# Revit family: Hager-VECTOR-Surface_mounted-IP65-With_Cover-With_DIN-NoHosted-PT-pt
name_source: partatom
category: Electrical Equipment
units: mm (PartAtom-declared; Revit-internal decimal feet)

## family parameters
Always vertical = Yes
Cut with Voids When Loaded = No
Maintain Annotation Orientation = No
Panel Configuration = Two Columns, Circuits Across
Part Type = Panelboard
Room Calculation Point = No
Round Connector Dimension = Use Diameter
Shared = No
Work Plane-Based = Yes

## types (22) — shared parameters
Code hager = ADD-EC000214_EU
Default Elevation = 1200 mm
EF000003 - Mounting method = Surface mounted
EF000024 - UV resistant = No
EF000116 - RAL-number = 7035
EF000118 - With mounting plate = No
EF001062 - EMC-version = No
EF001134 - DIN-rail = Yes
EF005474 - Degree of protection (IP) = IP65
EF006306 - With lock = No
EF015777 - Neutral terminal block = No
ETIM class code = EC000214
ETIM class name = Small distribution board
HG000001-Number of columns = 1
HG000002-With door or cover = Yes
HG000003-Range = VECTOR
HG000005-Thickness = 2 mm  [stored 0.00656168 ft]
HG000006-Flush mounted = No
HG000009-Double swing door = No
HG000010-Asymmetric doors = No
HG000011-Empty rows from bottom = No
HG000012-Door swing angle = 90.00°
HG000013-Door on the left = No
HG000014-Door on the right = Yes
HG000015-Clearance visibility = Yes
HG000016-Door 3D visibility = Yes
HG000017-Distance between poles = 18 mm  [stored 0.0590551 ft]
HG000060-RAL-number = 7035
HG000099-Onfly Template ID = 507532
Manufacturer = Hager
Name BIM&CO = Electricity
Name hager = ADD_Enclosures_EC000214
Reference = Template-Enclosure_EU-EC000214
Uniformat = Low Tension Service & Dist.
Uniformat code = D501001
zero-valued in all types: EF000218 - Built-in depth, EF000332 - Built-in height, EF000846 - Built-in width, EF001131 - Inner depth, HG000007-Number of empty columns, HG000008-Number of empty rows

## per-type parameters (varying)
| type | BC_METADATA | EF000007 - Colour | EF000008 - Width | EF000040 - Height | EF000049 - Depth | EF000266 - Number of rows | EF001088 - Extension possible | EF002950 - Width in number of modular spacings | EF004462 - Type of closure | EF006244 - Transparent cover/door | EF009212 - Cover model | EF015776 - Earthing terminal block | EF015941 - Signal passing door | HG000004-Manufacturer reference | HGEF000266-Number of rows | HGEF002950-Width in number of modular spacings |
| VECTOR-Surface_mounted_W111_H175_D93_3_Modular_Spacing-VE103F | {"ObjectGuid":"c818a3f8-cb3e-4e96-bf42-8305a581fb7f","ModelGuid":"de062844-ffcc-43d8-beb4-dd44a158ba7a","VariantGuid":"d379b219-8018-46ca-83cf-a631826d22f0","Revision":"#3","VariantName":"VECTOR-Surface_mounted_W111_H175_D93_3_Modular_Spacing-VE103F"} |  | 111 mm | 175 mm  [stored 0.574147 ft] | 93 mm  [stored 0.305118 ft] | 1 | No | 3 |  | No |  | No | No | VE103F | 1 | 3 |
| VECTOR-Surface_mounted_W111_H175_D93_3_Modular_Spacing-VE103PN | {"ObjectGuid":"c818a3f8-cb3e-4e96-bf42-8305a581fb7f","ModelGuid":"de062844-ffcc-43d8-beb4-dd44a158ba7a","VariantGuid":"1c7438d9-121e-4007-8086-bf25725793c4","Revision":"#3","VariantName":"VECTOR-Surface_mounted_W111_H175_D93_3_Modular_Spacing-VE103PN"} | Grey | 111 mm | 175 mm  [stored 0.574147 ft] | 93 mm  [stored 0.305118 ft] | 1 | Yes | 3 | Other | Yes | With notch | No | Yes | VE103PN | 1 | 3 |
| VECTOR-Surface_mounted_W111_H175_D93_3_Modular_Spacing-VE103SN | {"ObjectGuid":"c818a3f8-cb3e-4e96-bf42-8305a581fb7f","ModelGuid":"de062844-ffcc-43d8-beb4-dd44a158ba7a","VariantGuid":"c26a93cf-744a-48ef-bdf8-f0da6afd411e","Revision":"#3","VariantName":"VECTOR-Surface_mounted_W111_H175_D93_3_Modular_Spacing-VE103SN"} | Grey | 111 mm | 175 mm  [stored 0.574147 ft] | 93 mm  [stored 0.305118 ft] | 1 | Yes | 3 | Other | Yes | With notch | No | Yes | VE103SN | 1 | 3 |
| VECTOR-Surface_mounted_W165_H190_D113_6_Modular_Spacing-VE106F | {"ObjectGuid":"c818a3f8-cb3e-4e96-bf42-8305a581fb7f","ModelGuid":"de062844-ffcc-43d8-beb4-dd44a158ba7a","VariantGuid":"1c0c480d-506a-456c-ab41-44eb73c9ee99","Revision":"#3","VariantName":"VECTOR-Surface_mounted_W165_H190_D113_6_Modular_Spacing-VE106F"} | Grey | 165 mm | 190 mm  [stored 0.62336 ft] | 113 mm | 1 | Yes | 6 | Other | No | Closed | Yes | Yes | VE106F | 1 | 6 |
| VECTOR-Surface_mounted_W165_H190_D113_6_Modular_Spacing-VE106SN | {"ObjectGuid":"c818a3f8-cb3e-4e96-bf42-8305a581fb7f","ModelGuid":"de062844-ffcc-43d8-beb4-dd44a158ba7a","VariantGuid":"24822e05-d6b1-4cb1-8454-4b549ae1b19a","Revision":"#3","VariantName":"VECTOR-Surface_mounted_W165_H190_D113_6_Modular_Spacing-VE106SN"} | Grey | 165 mm | 190 mm  [stored 0.62336 ft] | 113 mm | 1 | Yes | 6 | Other | Yes | With notch | No | Yes | VE106SN | 1 | 6 |
| VECTOR-Surface_mounted_W237_H210_D114_10_Modular_Spacing-VE110F | {"ObjectGuid":"c818a3f8-cb3e-4e96-bf42-8305a581fb7f","ModelGuid":"de062844-ffcc-43d8-beb4-dd44a158ba7a","VariantGuid":"889c0ca8-4cfd-444d-b83f-5cb7c752534d","Revision":"#3","VariantName":"VECTOR-Surface_mounted_W237_H210_D114_10_Modular_Spacing-VE110F"} | Grey | 237 mm | 210 mm | 114 mm | 1 | Yes | 10 | Other | No | Closed | Yes | Yes | VE110F | 1 | 10 |
| VECTOR-Surface_mounted_W237_H210_D114_10_Modular_Spacing-VE110SN | {"ObjectGuid":"c818a3f8-cb3e-4e96-bf42-8305a581fb7f","ModelGuid":"de062844-ffcc-43d8-beb4-dd44a158ba7a","VariantGuid":"fce4fea5-d74b-4a0d-a7f3-c54e0f253287","Revision":"#3","VariantName":"VECTOR-Surface_mounted_W237_H210_D114_10_Modular_Spacing-VE110SN"} | Grey | 237 mm | 210 mm | 114 mm | 1 | Yes | 10 | Other | Yes | Closed | No | Yes | VE110SN | 1 | 10 |
| VECTOR-Surface_mounted_W310_H302_D151_12_Modular_Spacing-VE112F | {"ObjectGuid":"c818a3f8-cb3e-4e96-bf42-8305a581fb7f","ModelGuid":"de062844-ffcc-43d8-beb4-dd44a158ba7a","VariantGuid":"d7344623-fad3-43f5-b458-7f6c09bb8a48","Revision":"#3","VariantName":"VECTOR-Surface_mounted_W310_H302_D151_12_Modular_Spacing-VE112F"} | Grey | 310 mm | 302 mm | 151 mm | 1 | Yes | 12 | Other | No | Closed | Yes | Yes | VE112F | 1 | 12 |
| VECTOR-Surface_mounted_W310_H302_D151_12_Modular_Spacing-VE112SN | {"ObjectGuid":"c818a3f8-cb3e-4e96-bf42-8305a581fb7f","ModelGuid":"de062844-ffcc-43d8-beb4-dd44a158ba7a","VariantGuid":"6cdb95a3-8617-4916-8ba7-ceb8331fe390","Revision":"#3","VariantName":"VECTOR-Surface_mounted_W310_H302_D151_12_Modular_Spacing-VE112SN"} | Grey | 310 mm | 302 mm | 151 mm | 1 | Yes | 12 | Other | Yes | Closed | No | Yes | VE112SN | 1 | 12 |
| VECTOR-Surface_mounted_W418_H302_D151_18_Modular_Spacing-VE118F | {"ObjectGuid":"c818a3f8-cb3e-4e96-bf42-8305a581fb7f","ModelGuid":"de062844-ffcc-43d8-beb4-dd44a158ba7a","VariantGuid":"da2dd4eb-da4e-4338-b88a-964ffe794436","Revision":"#3","VariantName":"VECTOR-Surface_mounted_W418_H302_D151_18_Modular_Spacing-VE118F"} | Grey | 418 mm | 302 mm | 151 mm | 1 | No | 18 | Other | No | Closed | No | No | VE118F | 1 | 18 |
| VECTOR-Surface_mounted_W418_H302_D151_18_Modular_Spacing-VE118SN | {"ObjectGuid":"c818a3f8-cb3e-4e96-bf42-8305a581fb7f","ModelGuid":"de062844-ffcc-43d8-beb4-dd44a158ba7a","VariantGuid":"0fe867de-8f7d-414c-953e-5d8f91e5c74b","Revision":"#3","VariantName":"VECTOR-Surface_mounted_W418_H302_D151_18_Modular_Spacing-VE118SN"} | Grey | 418 mm | 302 mm | 151 mm | 1 | Yes | 18 | Other | Yes | Closed | No | Yes | VE118SN | 1 | 18 |
| VECTOR-Surface_mounted_W310_H427_D151_12_Modular_Spacing-VE212F | {"ObjectGuid":"c818a3f8-cb3e-4e96-bf42-8305a581fb7f","ModelGuid":"de062844-ffcc-43d8-beb4-dd44a158ba7a","VariantGuid":"72273de5-cad5-4311-bc03-508e701385d0","Revision":"#3","VariantName":"VECTOR-Surface_mounted_W310_H427_D151_12_Modular_Spacing-VE212F"} | Grey | 310 mm | 427 mm | 151 mm | 2 | Yes | 12 | Other | No | Closed | Yes | Yes | VE212F | 2 | 12 |
| VECTOR-Surface_mounted_W310_H427_D151_12_Modular_Spacing-VE212PN | {"ObjectGuid":"c818a3f8-cb3e-4e96-bf42-8305a581fb7f","ModelGuid":"de062844-ffcc-43d8-beb4-dd44a158ba7a","VariantGuid":"cc8b0d69-4bfc-4bcb-b978-dedab40a4ee9","Revision":"#3","VariantName":"VECTOR-Surface_mounted_W310_H427_D151_12_Modular_Spacing-VE212PN"} | Grey | 310 mm | 427 mm | 151 mm | 2 | Yes | 12 | Other | Yes | Closed | No | Yes | VE212PN | 2 | 12 |
| VECTOR-Surface_mounted_W310_H427_D151_12_Modular_Spacing-VE212SN | {"ObjectGuid":"c818a3f8-cb3e-4e96-bf42-8305a581fb7f","ModelGuid":"de062844-ffcc-43d8-beb4-dd44a158ba7a","VariantGuid":"bfaeb309-1490-4182-b2df-4f6d26c66b00","Revision":"#3","VariantName":"VECTOR-Surface_mounted_W310_H427_D151_12_Modular_Spacing-VE212SN"} | Grey | 310 mm | 427 mm | 151 mm | 2 | Yes | 12 | Other | Yes | Closed | No | Yes | VE212SN | 2 | 12 |
| VECTOR-Surface_mounted_W418_H452_D151_18_Modular_Spacing-VE218F | {"ObjectGuid":"c818a3f8-cb3e-4e96-bf42-8305a581fb7f","ModelGuid":"de062844-ffcc-43d8-beb4-dd44a158ba7a","VariantGuid":"dca828fc-dc95-4363-a96f-bb60e5068c5e","Revision":"#3","VariantName":"VECTOR-Surface_mounted_W418_H452_D151_18_Modular_Spacing-VE218F"} | Grey | 418 mm | 452 mm | 151 mm | 2 | No | 18 | Other | No | Closed | No | No | VE218F | 2 | 18 |
| VECTOR-Surface_mounted_W418_H452_D151_18_Modular_Spacing-VE218SN | {"ObjectGuid":"c818a3f8-cb3e-4e96-bf42-8305a581fb7f","ModelGuid":"de062844-ffcc-43d8-beb4-dd44a158ba7a","VariantGuid":"e732e4a5-a197-4b6b-b0f0-817f6099fd9c","Revision":"#3","VariantName":"VECTOR-Surface_mounted_W418_H452_D151_18_Modular_Spacing-VE218SN"} | Grey | 418 mm | 452 mm | 151 mm | 2 | Yes | 18 | Other | Yes | With notch | No | Yes | VE218SN | 2 | 18 |
| VECTOR-Surface_mounted_W310_H552_D151_12_Modular_Spacing-VE312F | {"ObjectGuid":"c818a3f8-cb3e-4e96-bf42-8305a581fb7f","ModelGuid":"de062844-ffcc-43d8-beb4-dd44a158ba7a","VariantGuid":"67d39e12-c837-4e2a-aee0-9534765b6384","Revision":"#3","VariantName":"VECTOR-Surface_mounted_W310_H552_D151_12_Modular_Spacing-VE312F"} | Grey | 310 mm | 552 mm | 151 mm | 3 | Yes | 12 | Other | No | Closed | Yes | Yes | VE312F | 3 | 12 |
| VECTOR-Surface_mounted_W310_H552_D151_12_Modular_Spacing-VE312SN | {"ObjectGuid":"c818a3f8-cb3e-4e96-bf42-8305a581fb7f","ModelGuid":"de062844-ffcc-43d8-beb4-dd44a158ba7a","VariantGuid":"60ea32ff-386f-455d-9f4e-3e8ea6d7304f","Revision":"#3","VariantName":"VECTOR-Surface_mounted_W310_H552_D151_12_Modular_Spacing-VE312SN"} | Grey | 310 mm | 552 mm | 151 mm | 3 | Yes | 12 | Other | Yes | With notch | No | Yes | VE312SN | 3 | 12 |
| VECTOR-Surface_mounted_W418_H602_D151_18_Modular_Spacing-VE318F | {"ObjectGuid":"c818a3f8-cb3e-4e96-bf42-8305a581fb7f","ModelGuid":"de062844-ffcc-43d8-beb4-dd44a158ba7a","VariantGuid":"5ef7dc98-6c9e-47ca-b5a4-a4ca5a36115d","Revision":"#3","VariantName":"VECTOR-Surface_mounted_W418_H602_D151_18_Modular_Spacing-VE318F"} | Grey | 418 mm | 602 mm | 151 mm | 3 | No | 18 | Other | No | With notch | No | No | VE318F | 3 | 18 |
| VECTOR-Surface_mounted_W418_H602_D151_18_Modular_Spacing-VE318SN | {"ObjectGuid":"c818a3f8-cb3e-4e96-bf42-8305a581fb7f","ModelGuid":"de062844-ffcc-43d8-beb4-dd44a158ba7a","VariantGuid":"c670ed9c-264b-4852-ae6a-bccfabafec5f","Revision":"#3","VariantName":"VECTOR-Surface_mounted_W418_H602_D151_18_Modular_Spacing-VE318SN"} | Grey | 418 mm | 602 mm | 151 mm | 3 | Yes | 18 | Other | Yes | With notch | No | Yes | VE318SN | 3 | 18 |
| VECTOR-Surface_mounted_W310_H677_D151_12_Modular_Spacing-VE412F | {"ObjectGuid":"c818a3f8-cb3e-4e96-bf42-8305a581fb7f","ModelGuid":"de062844-ffcc-43d8-beb4-dd44a158ba7a","VariantGuid":"15224343-c0c9-4e6e-b123-7119c932cf83","Revision":"#3","VariantName":"VECTOR-Surface_mounted_W310_H677_D151_12_Modular_Spacing-VE412F"} | Grey | 310 mm | 677 mm | 151 mm | 4 | No | 12 | Other | No | With notch | No | No | VE412F | 4 | 12 |
| VECTOR-Surface_mounted_W310_H677_D151_12_Modular_Spacing-VE412SN | {"ObjectGuid":"c818a3f8-cb3e-4e96-bf42-8305a581fb7f","ModelGuid":"de062844-ffcc-43d8-beb4-dd44a158ba7a","VariantGuid":"3a32f247-4032-4b6e-b4cc-89f2d7cb5545","Revision":"#3","VariantName":"VECTOR-Surface_mounted_W310_H677_D151_12_Modular_Spacing-VE412SN"} | Grey | 310 mm | 677 mm | 151 mm | 4 | Yes | 12 | Other | Yes | With notch | No | Yes | VE412SN | 4 | 12 |

note: [stored X ft] marks values corroborated as IEEE doubles in the binary element streams (Revit-internal decimal feet)

## geometry (parser evidence)
native form markers: Sweep x14
no freeform markers — native parametric forms only
